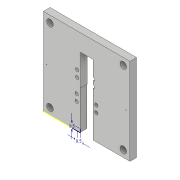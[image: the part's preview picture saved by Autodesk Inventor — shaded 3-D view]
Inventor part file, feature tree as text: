
AUTODESK INVENTOR PART (.ipt)
format: ipt  version: 2019 (Build 230136000, 136)  size: 189,440 bytes
history: native  units: in
note: dims shown in document units (in); Inventor stores cm internally (conversion verified against a paired STEP export)
features: sketch x12, extrude x9
ambient origin geometry x8: Origin, YZ Plane, XZ Plane, XY Plane, X Axis, Y Axis, Z Axis, Center Point
bodies: Solid1 (feature_tree)
feature tree (21):
  extrude  "Extrusion1"  Depth=5.1181in
  extrude  "Extrusion2"  Depth=0.3937in
  extrude  "Extrusion3"  Depth=0.3937in
  extrude  "Extrusion4"  Depth=4.3307in
  extrude  "Extrusion5"  Depth=0.3937in
  sketch  "Sketch6"  dims[d11=0.3937in d12=0.3937in]
  extrude  "Extrusion6"  Depth=0.3937in
  extrude  "Extrusion7"  TaperAngle=0.0deg  [1 undecoded]
  extrude  "Extrusion8"  Depth=0.1969in
  sketch  "Sketch10"  dims[d21=0.1969in]
  sketch  "Sketch11"  dims[d22=0.0039in]
  extrude  "Extrusion9"  TaperAngle=0.0deg  [1 undecoded]
  sketch  "Sketch1"  dims[d0=5.1181in d1=5.1181in]
  sketch  "Sketch2"  dims[d2=0.3937in d3=0.0in d4=0.3937in]
  sketch  "Sketch3"  dims[d5=4.3307in d6=0.3937in]
  sketch  "Sketch4"  dims[d7=4.3307in d8=4.3307in]
  sketch  "Sketch5"  dims[d9=4.3307in d10=0.3937in]
  sketch  "Sketch7"  dims[d13=0.3937in d14=0.0in d15=0.0in]
  sketch  "Sketch8"  dims[d16=0.1969in d17=0.1969in]
  sketch  "Sketch9"  dims[d18=0.0039in d19=0.0in d20=0.0in]
  sketch  "Sketch12"  dims[d23=0.3937in d24=0.0in d25=0.1969in d26=0.0394in d27=0.0394in d28=0.0in d29=0.0in d30=2.1654in d31=0.7874in d32=2.1654in d33=0.7874in d34=2.2835in d35=0.3937in d36=0.0in d37=0.1969in d38=1.4961in d39=0.3937in d40=0.1969in d41=1.4961in d42=0.3937in d43=0.1969in d44=0.1969in d45=0.1969in d46=0.1969in d47=0.0in d48=0.0in d49=0.3937in d50=0.0in d51=0.1969in d52=0.1969in d53=0.1969in d54=0.3937in d55=0.1969in d56=0.1969in d59=0.3937in d60=0.0in d61=0.0984in d62=0.1969in d64=0.1969in d65=0.1969in]
note: 2 required parameter values undecoded (feature->parameter linkage not recoverable at this tier; creation-order binding heuristic only, values carry confidence <= 0.55)
